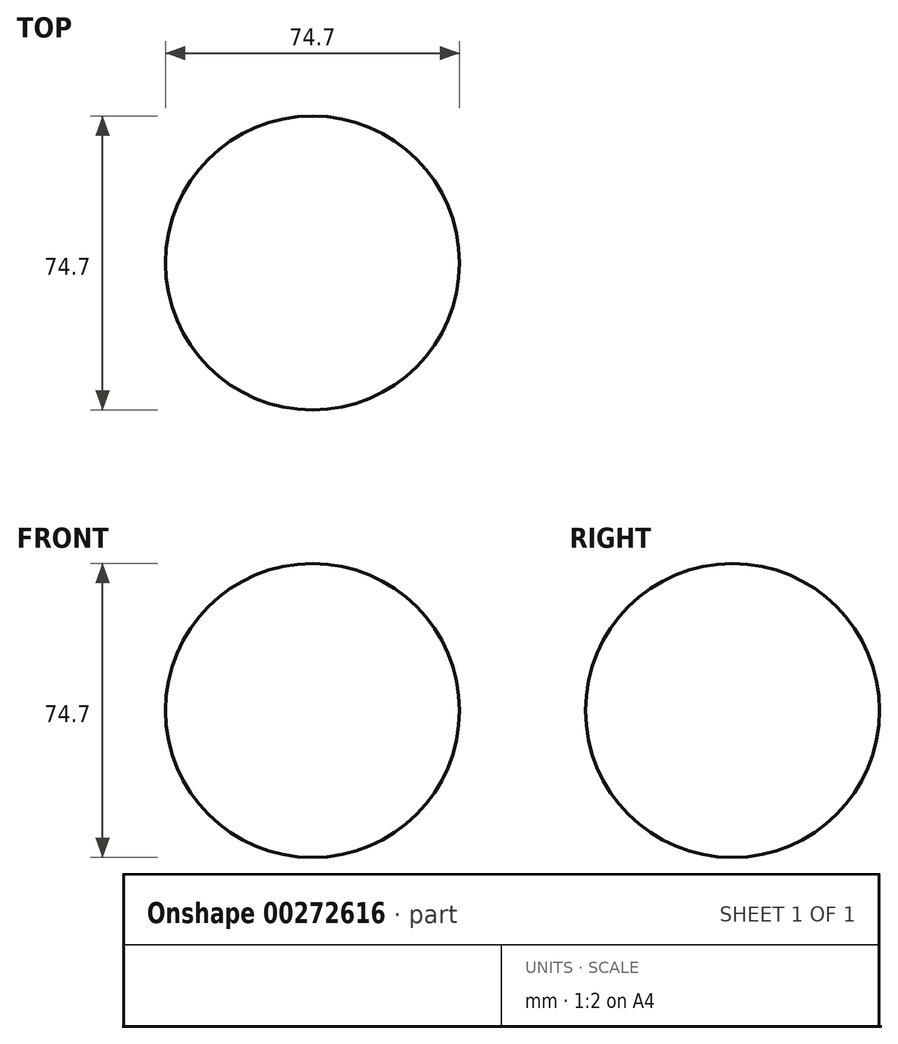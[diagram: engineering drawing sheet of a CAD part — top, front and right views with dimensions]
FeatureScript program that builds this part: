
annotation { "Feature Type Name" : "Feature", "Feature Type Description" : "" }
export const myFeature = defineFeature(function(context is Context, id is Id, definition is map)
    precondition{}
    {
        {
            var Q0;
            Q0=qCreatedBy(makeId("Front.planeOp"),FACE);
            var sketch = newSketch(context, id + "F0", { "sketchPlane" : qUnion([Q0])});
            skArc(sketch, "E0", {"start": v(0, 37.35) * mm, "mid": v(-37.35, 0) * mm, "end": v(0, -37.35) * mm});
            skLineSegment(sketch, "E1", {"start": v(0, 37.35) * mm, "end": v(0, -37.35) * mm});
            skSolve(sketch);
        }
        {
            var Q0;
            Q0=makeQuery(id+"F0.imprint","IMPRINT",FACE,{"disambiguationData":[TD([[makeQuery(id+"F0.imprint","IMPRINT",EDGE,{"derivedFrom":sQuery(id+"F0.wireOp",EDGE,"E0")}),1.0]])]});
            var Q1;
            Q1=sQuery(id+"F0.wireOp",EDGE,"E1");
            revolve(context, id + "F1", {"entities" : qUnion([Q0]), "axis" : qUnion([Q1]), "revolveType" : RevolveType.FULL});
        }
    });
